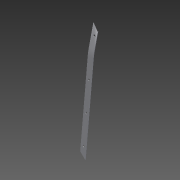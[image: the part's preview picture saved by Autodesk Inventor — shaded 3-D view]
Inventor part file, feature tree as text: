
AUTODESK INVENTOR PART (.ipt)
format: ipt  version: 2015 (Build 190159000, 159)  size: 138,240 bytes
history: native  units: mm
features: reference x9, sketch x6, other x3, extrude x2, sweep x1, hole x1
ambient origin geometry x8: Origin, YZ Plane, XZ Plane, XY Plane, X Axis, Y Axis, Z Axis, Center Point
bodies: Body1 (feature_tree)
feature tree (22):
  other  "Listwa_siedziska_prawa"
  sweep  "Przeciągnięcie1"
  sketch  "Szkic2"
  other  "Gięcie części1"
  extrude  "Wyciągnięcie proste3"  Depth=1.5mm
  extrude  "Wyciągnięcie proste4"  Depth=1.22173mm
  hole  "Otwór2"  [1 undecoded]
  sketch  "Szkic1"
  sketch  "Szkic4"
  sketch  "Szkic5"
  other  "Bryła2"
  sketch  "Szkic6"
  reference  "Odniesienie1"
  sketch  "Szkic7"
  reference  "Odniesienie2"
  reference  "Odniesienie3"
  reference  "Odniesienie4"
  reference  "Odniesienie5"
  reference  "Odniesienie6"
  reference  "Odniesienie7"
  reference  "Odniesienie8"
  reference  "Odniesienie9"
note: 1 required parameter value undecoded (feature->parameter linkage not recoverable at this tier; creation-order binding heuristic only, values carry confidence <= 0.55)
